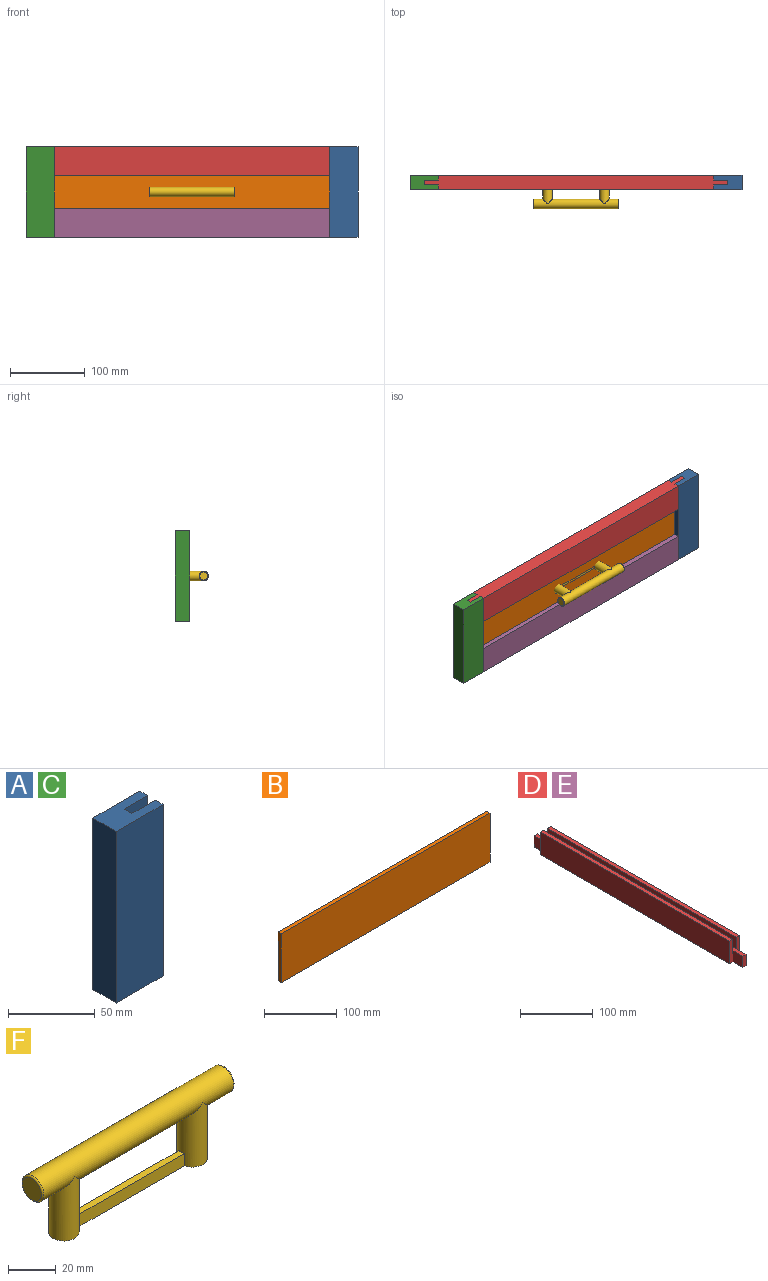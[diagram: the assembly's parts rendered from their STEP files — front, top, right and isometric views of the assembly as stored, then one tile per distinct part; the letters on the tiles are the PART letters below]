
ASSEMBLY  parts=6 mates=5
PART A: 10 faces, bbox 38.1x19.1x120.7 mm
  f0: plane 120.65x6.35mm, normal (1,0,0), area 766.1mm2, adj f4,f5,f6,f7
  f1: plane 120.65x19.05mm, normal (-1,0,0), area 2298.4mm2, adj f2,f4,f5,f6
  f2: plane 120.65x38.1mm, normal (0,-1,0), area 4596.8mm2, adj f1,f3,f5,f6
  f3: plane 120.65x6.35mm, normal (1,0,0), area 766.1mm2, adj f2,f5,f6,f9
  f4: plane 120.65x38.1mm, normal (0,1,0), area 4596.8mm2, adj f0,f1,f5,f6
  f5: plane 38.1x19.05mm, normal (0,0,1), area 604.8mm2, adj f0,f1,f2,f3,f4,f7,f8,f9
  f6: plane 38.1x19.05mm, normal (0,0,-1), area 604.8mm2, adj f0,f1,f2,f3,f4,f7,f8,f9
  f7: plane 120.65x19.05mm, normal (0,-1,0), area 2298.4mm2, adj f0,f5,f6,f8
  f8: plane 120.65x6.35mm, normal (1,0,0), area 766.1mm2, adj f5,f6,f7,f9
  f9: plane 120.65x19.05mm, normal (0,1,0), area 2298.4mm2, adj f3,f5,f6,f8
PART B: 6 faces, bbox 406.4x6.4x82.6 mm
  f0: plane 82.55x6.35mm, normal (-1,0,0), area 524.2mm2, adj f1,f3,f4,f5
  f1: plane 406.4x6.35mm, normal (0,0,-1), area 2580.6mm2, adj f0,f2,f4,f5
  f2: plane 82.55x6.35mm, normal (1,0,0), area 524.2mm2, adj f1,f3,f4,f5
  f3: plane 406.4x6.35mm, normal (0,0,1), area 2580.6mm2, adj f0,f2,f4,f5
  f4: plane 406.4x82.55mm, normal (0,-1,0), area 33548.3mm2, adj f0,f1,f2,f3
  f5: plane 406.4x82.55mm, normal (0,1,0), area 33548.3mm2, adj f0,f1,f2,f3
PART C: same geometry as A
PART D: 18 faces, bbox 19.1x406.4x38.1 mm
  f0: plane 368.3x6.35mm, normal (0,0,1), area 2338.7mm2, adj f4,f6,f10,f15
  f1: plane 19.05x6.35mm, normal (0,1,0), area 121mm2, adj f8,f9,f14,f17
  f2: plane 19.05x6.35mm, normal (0,-1,0), area 121mm2, adj f8,f9,f11,f13
  f3: plane 368.3x38.1mm, normal (-1,0,0), area 14032.2mm2, adj f5,f8,f12,f16
  f4: plane 368.3x38.1mm, normal (1,0,0), area 14032.2mm2, adj f0,f8,f10,f15
  f5: plane 368.3x6.35mm, normal (0,0,1), area 2338.7mm2, adj f3,f7,f12,f16
  f6: plane 368.3x19.05mm, normal (-1,0,0), area 7016.1mm2, adj f0,f9,f10,f15
  f7: plane 368.3x19.05mm, normal (1,0,0), area 7016.1mm2, adj f5,f9,f12,f16
  f8: plane 406.4x19.05mm, normal (0,0,-1), area 7258mm2, adj f1,f2,f3,f4,f10,f11,f12,f13
  f9: plane 406.4x6.35mm, normal (0,0,1), area 2580.6mm2, adj f1,f2,f6,f7,f11,f13,f14,f17
  f10: plane 38.1x6.35mm, normal (0,-1,0), area 241.9mm2, adj f0,f4,f6,f8,f11
  f11: plane 19.05x19.05mm, normal (1,0,0), area 362.9mm2, adj f2,f8,f9,f10
  f12: plane 38.1x6.35mm, normal (0,-1,0), area 241.9mm2, adj f3,f5,f7,f8,f13
  f13: plane 19.05x19.05mm, normal (-1,0,0), area 362.9mm2, adj f2,f8,f9,f12
  f14: plane 19.05x19.05mm, normal (1,0,0), area 362.9mm2, adj f1,f8,f9,f15
  f15: plane 38.1x6.35mm, normal (0,1,0), area 241.9mm2, adj f0,f4,f6,f8,f14
  f16: plane 38.1x6.35mm, normal (0,1,0), area 241.9mm2, adj f3,f5,f7,f8,f17
  f17: plane 19.05x19.05mm, normal (-1,0,0), area 362.9mm2, adj f1,f8,f9,f16
PART E: same geometry as D
PART F: 15 faces, bbox 114.3x13.7x38.6 mm
  f0: cylinder r=6.35mm len=31.75mm, axis (0,0,-1), area 1085.1mm2, adj f1,f2,f6,f7,f8
  f1: plane 88.9x12.7mm, normal (0,0,-1), area 460.4mm2, adj f0,f3,f6,f7,f12,f13,f14
  f2: cylinder r=6.35mm len=112.71mm, axis (-1,0,0), area 4174.4mm2, adj f0,f3,f9,f10
  f3: cylinder r=6.35mm len=31.75mm, axis (0,0,-1), area 1085.1mm2, adj f1,f2,f6,f7,f8
  f4: plane 11.11x11.11mm, normal (1,0,0), area 97mm2, adj f10
  f5: plane 11.11x11.11mm, normal (-1,0,0), area 97mm2, adj f9
  f6: plane 63.9x6.35mm, normal (0,-1,0), area 405.8mm2, adj f0,f1,f3,f8
  f7: plane 63.9x6.35mm, normal (0,1,0), area 395.7mm2, adj f0,f1,f3,f8,f11,f12,f13
  f8: plane 63.9x3.18mm, normal (0,0,1), area 202mm2, adj f0,f3,f6,f7
  f9: torus R=5.56mm, axis (1,0,0), area 47.5mm2, adj f2,f5
  f10: torus R=5.56mm, axis (1,0,0), area 47.5mm2, adj f2,f4
  f11: plane 3.18x1.59mm, normal (0,0,1), area 5mm2, adj f7,f12,f13,f14
  f12: plane 3.18x1.59mm, normal (1,0,0), area 5mm2, adj f1,f7,f11,f14
  f13: plane 3.18x1.59mm, normal (-1,0,0), area 5mm2, adj f1,f7,f11,f14
  f14: plane 3.18x3.18mm, normal (0,1,0), area 10.1mm2, adj f1,f11,f12,f13
PLACE A rot(axis=(0,0,1),180deg) t=(444.5,19.05,0)mm
PLACE B t=(19.05,12.7,19.05)mm
PLACE C at identity
PLACE D rot(axis=(0.71,0.71,0),180deg) t=(425.45,0,120.65)mm
PLACE E rot(axis=(0,0,-1),90deg) t=(425.45,19.05,0)mm
PLACE F rot(axis=(1,0,0),90deg) t=(222.25,12.7,60.32)mm
MATE fastened A.f8 <-> D.f1  axis (-1,0,0) through (425.45,9.53,120.65)mm
MATE fastened B.f0 <-> C.f8  axis (-1,0,0) through (19.05,9.53,60.32)mm
MATE fastened F.f8 <-> B.f4  axis (0,-1,0) through (222.25,6.35,60.32)mm
MATE fastened E.f2 <-> C.f8  axis (-1,0,0) through (19.05,9.53,0)mm
MATE fastened D.f2 <-> C.f8  axis (-1,0,0) through (19.05,9.52,120.65)mm
